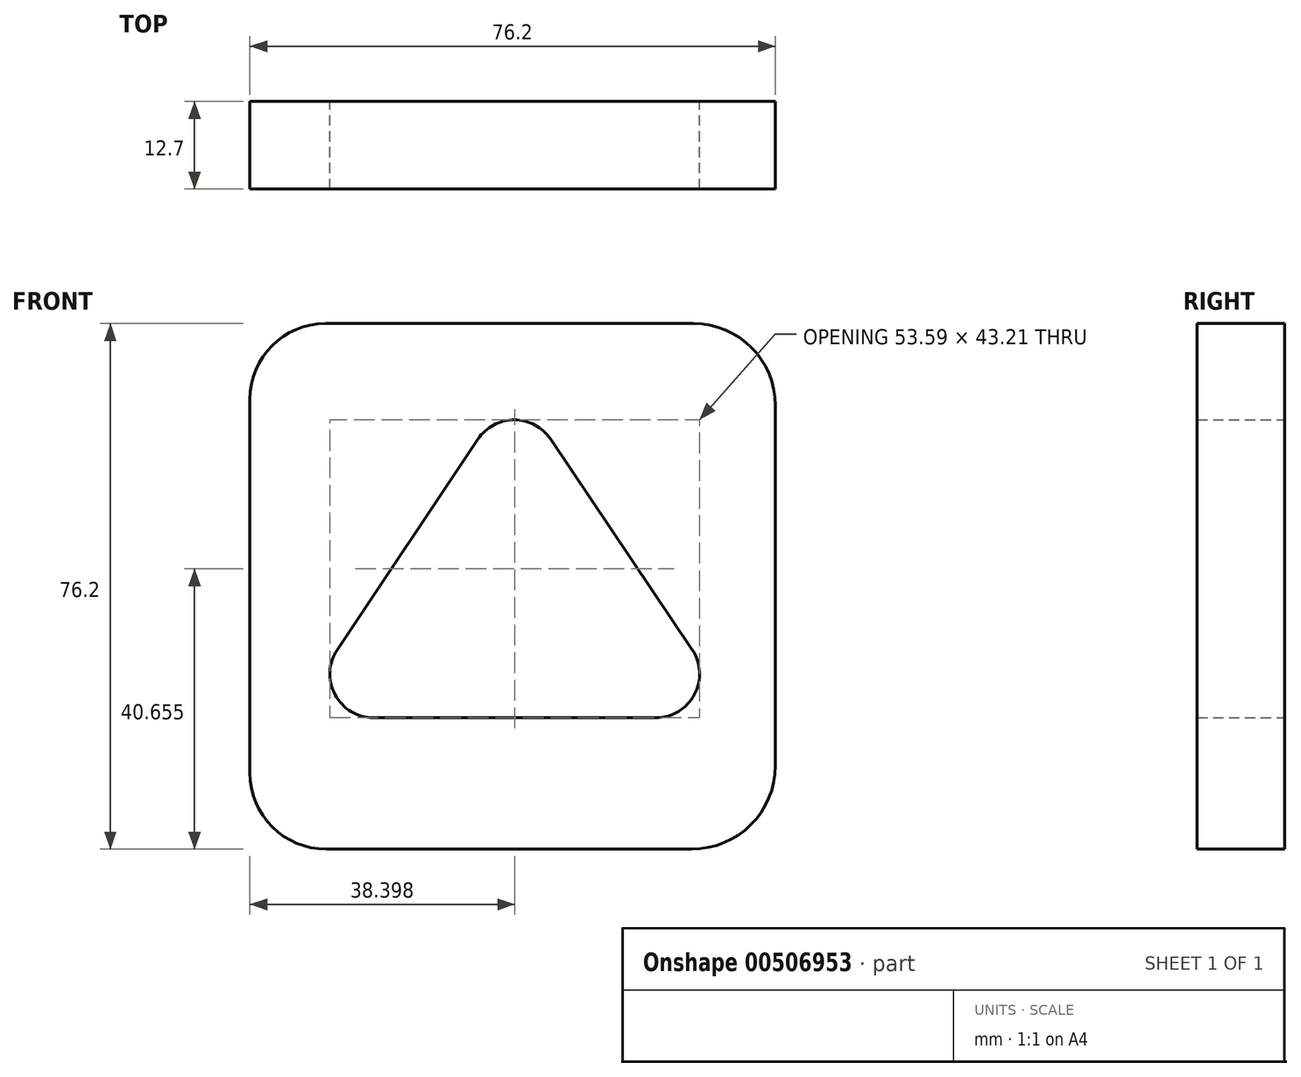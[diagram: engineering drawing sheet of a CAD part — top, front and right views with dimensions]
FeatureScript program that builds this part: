
annotation { "Feature Type Name" : "Feature", "Feature Type Description" : "" }
export const myFeature = defineFeature(function(context is Context, id is Id, definition is map)
    precondition{}
    {
        {
            var Q0;
            Q0=qCreatedBy(makeId("Front.planeOp"),FACE);
            var sketch = newSketch(context, id + "F0", { "sketchPlane" : qUnion([Q0])});
            skLineSegment(sketch, "E0", {"start": v(11.07, 0) * mm, "end": v(64.05, 0) * mm});
            skLineSegment(sketch, "E1", {"start": v(76.2, 12.15) * mm, "end": v(76.2, 64.32) * mm});
            skLineSegment(sketch, "E2", {"start": v(10.95, 76.2) * mm, "end": v(64.32, 76.2) * mm});
            skPoint(sketch, "E3.startSnap0", {"position": v(76.2, 38.1) * mm});
            skArc(sketch, "E4", {"start": v(12.66, 28.93) * mm, "mid": v(12.34, 22.4) * mm, "end": v(17.94, 19.05) * mm});
            skArc(sketch, "E5", {"start": v(43.6, 59.45) * mm, "mid": v(38.33, 62.26) * mm, "end": v(33.06, 59.44) * mm});
            skArc(sketch, "E6", {"start": v(58.85, 19.05) * mm, "mid": v(64.46, 22.41) * mm, "end": v(64.12, 28.94) * mm});
            skLineSegment(sketch, "E7", {"start": v(0, -13.56) * mm, "end": v(19.05, -13.56) * mm});
            skLineSegment(sketch, "E8", {"start": v(49.55, -13.2) * mm, "end": v(68.6, -13.2) * mm});
            skLineSegment(sketch, "E9", {"start": v(86.71, 25.4) * mm, "end": v(86.71, 0) * mm});
            skLineSegment(sketch, "E10", {"start": v(17.94, 19.05) * mm, "end": v(58.85, 19.05) * mm});
            skLineSegment(sketch, "E11", {"start": v(12.66, 28.93) * mm, "end": v(33.06, 59.44) * mm});
            skLineSegment(sketch, "E12", {"start": v(43.6, 59.45) * mm, "end": v(64.12, 28.94) * mm});
            skArc(sketch, "E13", {"start": v(0, 11.07) * mm, "mid": v(3.24, 3.24) * mm, "end": v(11.07, 0) * mm});
            skArc(sketch, "E14", {"start": v(76.2, 64.32) * mm, "mid": v(72.72, 72.72) * mm, "end": v(64.32, 76.2) * mm});
            skArc(sketch, "E15", {"start": v(64.05, 0) * mm, "mid": v(72.64, 3.56) * mm, "end": v(76.2, 12.15) * mm});
            skPoint(sketch, "E16.orphan", {"position": v(76.2, 0) * mm});
            skPoint(sketch, "E17.orphan", {"position": v(76.2, 76.2) * mm});
            skLineSegment(sketch, "E18", {"start": v(0, 65.25) * mm, "end": v(0, 11.07) * mm});
            skArc(sketch, "E19", {"start": v(10.95, 76.2) * mm, "mid": v(3.2, 73) * mm, "end": v(0, 65.25) * mm});
            skPoint(sketch, "E20.orphan", {"position": v(0, 76.2) * mm});
            skSolve(sketch);
        }
        {
            var Q0;
            Q0=makeQuery(id+"F0.imprint","IMPRINT",FACE,{"disambiguationData":[TD([[makeQuery(id+"F0.imprint","IMPRINT",EDGE,{"derivedFrom":sQuery(id+"F0.wireOp",EDGE,"E0")}),1.0]])]});
            extrude(context, id + "F1", {"entities" : qUnion([Q0]), "depth" : 12.7 * mm});
        }
    });
